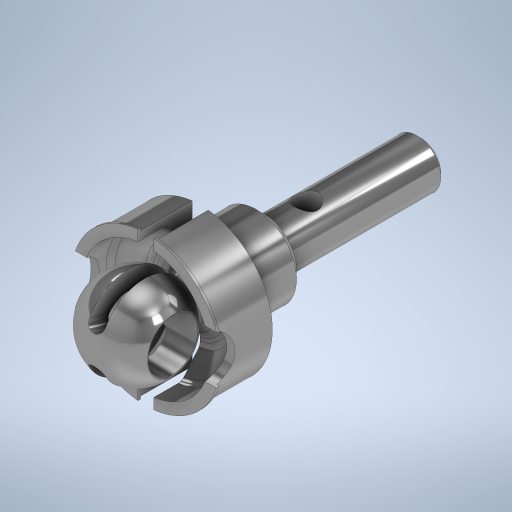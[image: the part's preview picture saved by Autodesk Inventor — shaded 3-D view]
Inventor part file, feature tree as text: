
AUTODESK INVENTOR PART (.ipt)
format: ipt  version: 2024 (Build 280153000, 153)  size: 633,344 bytes
history: native  units: in
note: dims shown in document units (in); Inventor stores cm internally (conversion verified against a paired STEP export)
features: sketch x7, extrude x5, chamfer x3, revolve x2, fillet x2, other x2, plane x1, mirror x1, thread x1, direct_edit x1
ambient origin geometry x8: Origin, YZ Plane, XZ Plane, XY Plane, X Axis, Y Axis, Z Axis, Center Point
bodies: Solid1 (feature_tree)
feature tree (25):
  extrude  "Extrusion1"  Depth=0.86in TaperAngle=0.0deg
  extrude  "Extrusion2"  Depth=0.15in
  chamfer  "Chamfer1"  Distance=0.015in Angle=45.0deg
  revolve  "Revolution1"  [1 undecoded]
  fillet  "Fillet1"  Radius=0.01in
  fillet  "Fillet2"  Radius=0.2125in
  extrude  "Extrusion3"  Depth=0.032in
  chamfer  "Chamfer2"  Angle=90.0deg  [1 undecoded]
  plane  "Work Plane1"
  revolve  "Revolution2"  [1 undecoded]
  mirror  "Mirror1"
  extrude  "Extrusion4"  Depth=0.3937in
  chamfer  "Chamfer3"  Distance=0.315in
  extrude  "Extrusion5"  Depth=0.3937in TaperAngle=0.0deg
  thread  "Thread1"  [1 undecoded]
  direct_edit  "Direct Edit1"
  sketch  "Sketch1"  dims[d0=0.1875in d1=0.86in d2=0.0in]
  sketch  "Sketch2"  dims[d3=0.3in d4=0.15in d5=-0.2749in d6=0.015in d7=0.125in d8=45.0deg]
  sketch  "Sketch3"  dims[d9=0.2812in d10=0.01in d11=0.01in d12=0.2125in]
  sketch  "Sketch4"  dims[d13=0.032in d14=0.032in]
  other  "Work Point1"
  sketch  "Sketch5"  dims[d15=0.1in]
  sketch  "Sketch6"  dims[d16=0.35in]
  sketch  "Sketch7"  dims[d17=0.1in d18=90.0deg d19=0.02in d20=0.032in d21=0.315in d22=0.25in d23=0.0in d24=0.032in d25=0.125in d26=45.0deg d27=0.0625in d28=0.5in d29=0.56in d30=90.0deg d31=0.2in d32=2.0in d33=0.0in d34=0.005in d35=0.125in d36=45.0deg d37=0.094in d38=0.448in d39=2.0in d40=0.0in d41=0.375in d42=0.0in d43=3.937in d44=0.3937in d45=0.3937in]
  other  "Scale1"
note: 4 required parameter values undecoded (feature->parameter linkage not recoverable at this tier; creation-order binding heuristic only, values carry confidence <= 0.55)